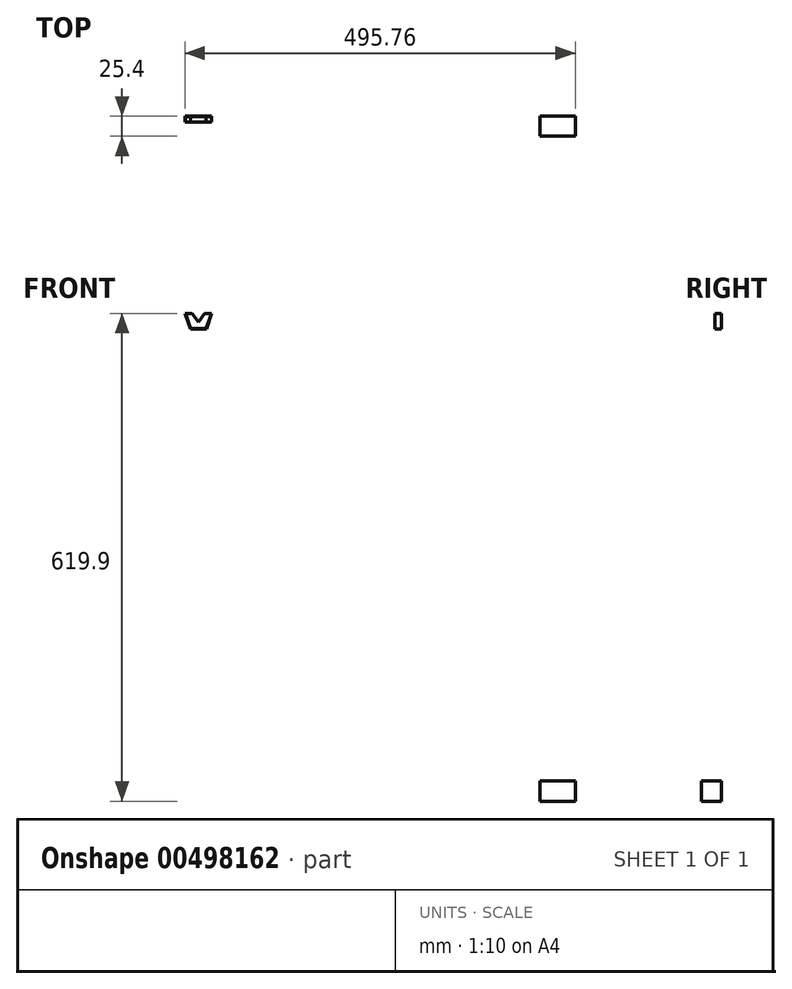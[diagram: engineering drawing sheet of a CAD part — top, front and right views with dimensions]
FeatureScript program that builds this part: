
annotation { "Feature Type Name" : "Feature", "Feature Type Description" : "" }
export const myFeature = defineFeature(function(context is Context, id is Id, definition is map)
    precondition{}
    {
        {
            var Q0;
            Q0=qCreatedBy(makeId("Front.planeOp"),FACE);
            var sketch = newSketch(context, id + "F0", { "sketchPlane" : qUnion([Q0])});
            skLineSegment(sketch, "E0.bottom", {"start": v(0, 3.17) * mm, "end": v(-45.04, 3.17) * mm});
            skLineSegment(sketch, "E0.top", {"start": v(0, 29.07) * mm, "end": v(-45.04, 29.07) * mm});
            skLineSegment(sketch, "E0.left", {"start": v(0, 3.17) * mm, "end": v(0, 29.07) * mm});
            skLineSegment(sketch, "E0.right", {"start": v(-45.04, 3.17) * mm, "end": v(-45.04, 29.07) * mm});
            skPoint(sketch, "E0.middle", {"position": v(-22.52, 16.12) * mm});
            skSolve(sketch);
        }
        {
            var Q0;
            Q0=makeQuery(id+"F0.imprint","IMPRINT",FACE,{"disambiguationData":[TD([[makeQuery(id+"F0.imprint","IMPRINT",EDGE,{"derivedFrom":sQuery(id+"F0.wireOp",EDGE,"E0.bottom")}),-1.0]])]});
            extrude(context, id + "F1", {"entities" : qUnion([Q0]), "depth" : 25.4 * mm});
        }
        {
            var Q0;
            Q0=qCreatedBy(makeId("Front.planeOp"),FACE);
            var sketch = newSketch(context, id + "F2", { "sketchPlane" : qUnion([Q0])});
            skLineSegment(sketch, "E1", {"start": v(-488.86, 603.24) * mm, "end": v(-468.66, 603.24) * mm});
            skLineSegment(sketch, "E2", {"start": v(-468.66, 603.24) * mm, "end": v(-461.76, 623.07) * mm});
            skLineSegment(sketch, "E3", {"start": v(-488.86, 603.24) * mm, "end": v(-495.76, 623.07) * mm});
            skLineSegment(sketch, "E4", {"start": v(-495.76, 623.07) * mm, "end": v(-486.76, 623.07) * mm});
            skPoint(sketch, "E5", {"position": v(-478.76, 612.32) * mm});
            skLineSegment(sketch, "E6", {"start": v(-486.76, 623.07) * mm, "end": v(-478.76, 612.32) * mm});
            skLineSegment(sketch, "E7", {"start": v(-470.76, 623.07) * mm, "end": v(-478.76, 612.32) * mm});
            skLineSegment(sketch, "E8.trimOffspring", {"start": v(-470.76, 623.07) * mm, "end": v(-461.76, 623.07) * mm});
            skSolve(sketch);
        }
        {
            var Q0;
            Q0=makeQuery(id+"F2.imprint","IMPRINT",FACE,{"disambiguationData":[TD([[makeQuery(id+"F2.imprint","IMPRINT",EDGE,{"derivedFrom":sQuery(id+"F2.wireOp",EDGE,"E1")}),1.0]])]});
            extrude(context, id + "F3", {"entities" : qUnion([Q0]), "depth" : 7.7 * mm});
        }
        {
            var Q0;
            Q0=makeQuery(id+"F3.opExtrude","SWEPT_FACE",FACE,{"disambiguationData":[OSD([sQuery(id+"F2.wireOp",EDGE,"E8.trimOffspring")])]});
            var Q1;
            Q1=makeQuery(id+"F3.opExtrude","SWEPT_FACE",FACE,{"disambiguationData":[OSD([sQuery(id+"F2.wireOp",EDGE,"E7")])]});
            var Q2;
            Q2=makeQuery(id+"F3.opExtrude","CAP_FACE",FACE,{"disambiguationData":[OSD([sQuery(id+"F2.wireOp",EDGE,"E1"),sQuery(id+"F2.wireOp",EDGE,"E2"),sQuery(id+"F2.wireOp",EDGE,"E3"),sQuery(id+"F2.wireOp",EDGE,"E4"),sQuery(id+"F2.wireOp",EDGE,"E6"),sQuery(id+"F2.wireOp",EDGE,"E7"),sQuery(id+"F2.wireOp",EDGE,"E8.trimOffspring")])],"isStart":false});
            var Q3;
            Q3=makeQuery(id+"F3.opExtrude","SWEPT_FACE",FACE,{"disambiguationData":[OSD([sQuery(id+"F2.wireOp",EDGE,"E4")])]});
            var Q4;
            Q4=makeQuery(id+"F3.opExtrude","SWEPT_FACE",FACE,{"disambiguationData":[OSD([sQuery(id+"F2.wireOp",EDGE,"E6")])]});
            shell(context, id + "F4", {"entities" : qUnion([Q0, Q1, Q2, Q3, Q4]), "thickness" : .5293 * mm});
        }
    });
